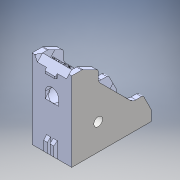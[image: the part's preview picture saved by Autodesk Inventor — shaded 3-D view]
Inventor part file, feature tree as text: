
AUTODESK INVENTOR PART (.ipt)
format: ipt  version: 2018 (Build 220112000, 112)  size: 875,008 bytes
history: native  units: mm
features: other x5, extrude x2, sketch x2, projected_geometry x1
ambient origin geometry x8: Origin, YZ Plane, XZ Plane, XY Plane, X Axis, Y Axis, Z Axis, Center Point
bodies: Body1 (feature_tree)
feature tree (10):
  other  "ソリッド1"
  other  "作業平面1"
  extrude  "押し出し1"  [1 undecoded]
  other  "作業平面2"
  other  "作業平面3"
  extrude  "押し出し2"  Depth=1.0mm TaperAngle=0.0deg
  sketch  "スケッチ1"
  sketch  "スケッチ2"
  projected_geometry  "投影ループ1"
  other  "ABLD-20-4-T"
note: 1 required parameter value undecoded (feature->parameter linkage not recoverable at this tier; creation-order binding heuristic only, values carry confidence <= 0.55)
